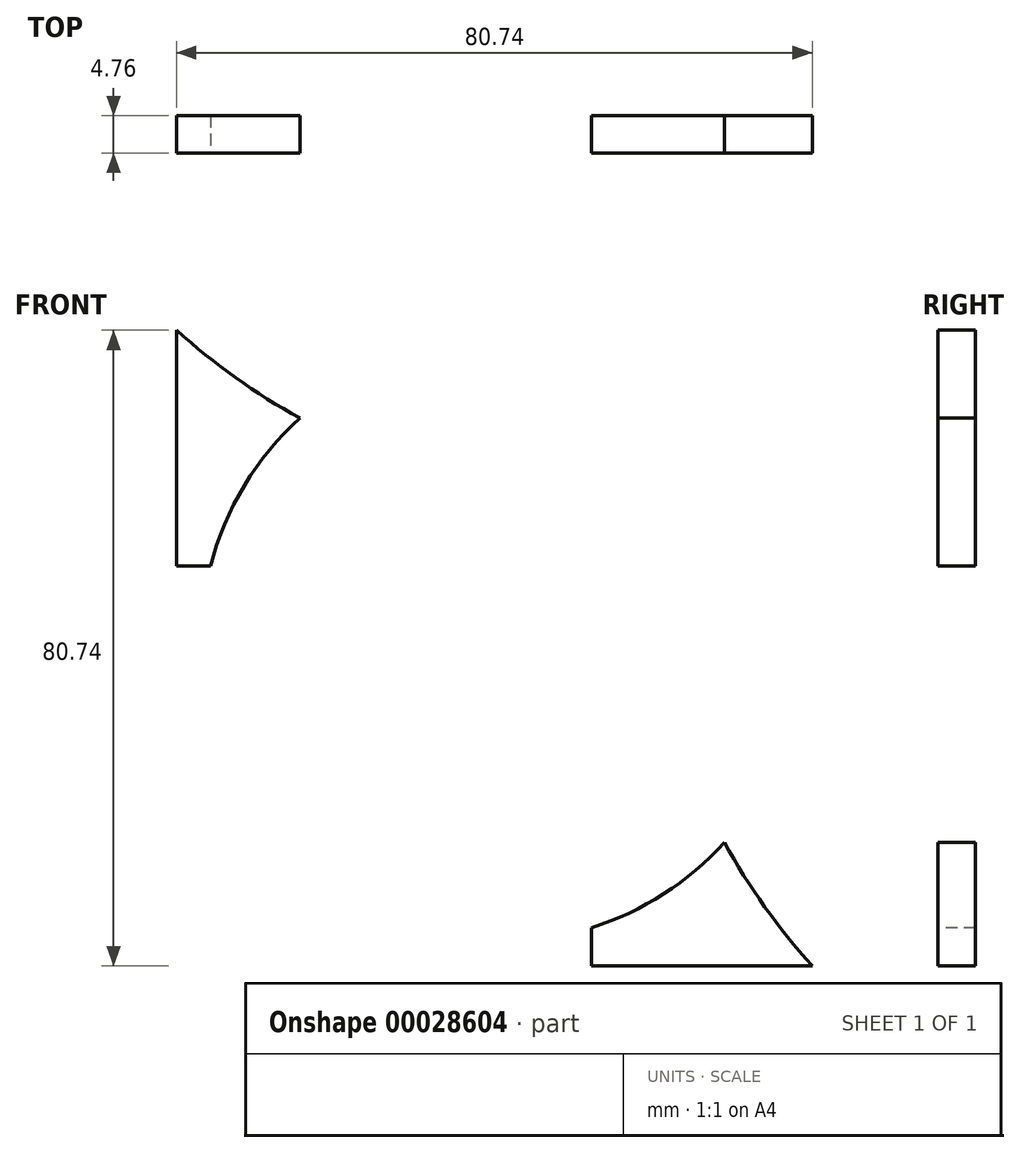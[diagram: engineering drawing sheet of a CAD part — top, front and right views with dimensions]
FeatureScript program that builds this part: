
annotation { "Feature Type Name" : "Feature", "Feature Type Description" : "" }
export const myFeature = defineFeature(function(context is Context, id is Id, definition is map)
    precondition{}
    {
        {
            var Q0;
            Q0=qCreatedBy(makeId("Front.planeOp"),FACE);
            var sketch = newSketch(context, id + "F0", { "sketchPlane" : qUnion([Q0])});
            skLineSegment(sketch, "E0.bottom", {"start": v(0, 0) * mm, "end": v(120.65, 0) * mm});
            skLineSegment(sketch, "E0.top", {"start": v(0, 120.65) * mm, "end": v(25.4, 120.65) * mm});
            skLineSegment(sketch, "E0.left", {"start": v(0, 0) * mm, "end": v(0, 120.65) * mm});
            skLineSegment(sketch, "E0.right", {"start": v(120.65, 0) * mm, "end": v(120.65, 25.4) * mm});
            skCircle(sketch, "E1", {"center": v(60.33, 60.33) * mm, "radius": 26.75 * mm});
            skArc(sketch, "E2", {"start": v(98.13, 65.62) * mm, "mid": v(87.32, 87.32) * mm, "end": v(65.62, 98.13) * mm});
            skArc(sketch, "E3", {"start": v(25.4, 120.65) * mm, "mid": v(43.4, 105.61) * mm, "end": v(65.62, 98.13) * mm});
            skArc(sketch, "E4", {"start": v(98.13, 65.62) * mm, "mid": v(105.61, 43.4) * mm, "end": v(120.65, 25.4) * mm});
            skPoint(sketch, "E5", {"position": v(25.4, 120.65) * mm});
            skPoint(sketch, "E6", {"position": v(120.65, 25.4) * mm});
            skSolve(sketch);
        }
        {
            var Q0;
            Q0=makeQuery(id+"F0.imprint","IMPRINT",FACE,{"disambiguationData":[TD([[makeQuery(id+"F0.imprint","IMPRINT",EDGE,{"derivedFrom":sQuery(id+"F0.wireOp",EDGE,"E0.bottom")}),1.0]])]});
            extrude(context, id + "F1", {"entities" : qUnion([Q0]), "depth" : 4.76 * mm});
        }
        {
            var Q0;
            Q0=makeQuery(id+"F1.opExtrude","CAP_FACE",FACE,{"disambiguationData":[OSD([sQuery(id+"F0.wireOp",EDGE,"E0.bottom"),sQuery(id+"F0.wireOp",EDGE,"E0.top"),sQuery(id+"F0.wireOp",EDGE,"E0.left"),sQuery(id+"F0.wireOp",EDGE,"E0.right"),sQuery(id+"F0.wireOp",EDGE,"E1"),sQuery(id+"F0.wireOp",EDGE,"E2"),sQuery(id+"F0.wireOp",EDGE,"E3"),sQuery(id+"F0.wireOp",EDGE,"E4")])],"isStart":false});
            var sketch = newSketch(context, id + "F2", { "sketchPlane" : qUnion([Q0])});
            skLineSegment(sketch, "E7", {"start": v(12.7, 114.3) * mm, "end": v(12.7, 12.7) * mm});
            skLineSegment(sketch, "E8", {"start": v(12.7, 12.7) * mm, "end": v(114.3, 12.7) * mm});
            skPoint(sketch, "E9", {"position": v(12.7, 88.9) * mm});
            skPoint(sketch, "E10", {"position": v(88.9, 12.7) * mm});
            skPoint(sketch, "E11", {"position": v(12.7, 63.5) * mm});
            skPoint(sketch, "E12", {"position": v(63.5, 12.7) * mm});
            skSolve(sketch);
        }
        {
            var Q0;
            Q0=sQuery(id+"F2.wireOp",VERTEX,"E9");
            var Q1;
            Q1=sQuery(id+"F2.wireOp",VERTEX,"E7.start");
            var Q2;
            Q2=sQuery(id+"F2.wireOp",VERTEX,"E11");
            var Q3;
            Q3=sQuery(id+"F2.wireOp",VERTEX,"E8.start");
            var Q4;
            Q4=sQuery(id+"F2.wireOp",VERTEX,"E12");
            var Q5;
            Q5=sQuery(id+"F2.wireOp",VERTEX,"E10");
            var Q6;
            Q6=sQuery(id+"F2.wireOp",VERTEX,"E8.end");
            var Q7;
            Q7=makeQuery(id+"F1.opExtrude","SWEPT_BODY",BODY,{"disambiguationData":[OSD([sQuery(id+"F0.wireOp",EDGE,"E0.bottom"),sQuery(id+"F0.wireOp",EDGE,"E0.top"),sQuery(id+"F0.wireOp",EDGE,"E0.left"),sQuery(id+"F0.wireOp",EDGE,"E0.right"),sQuery(id+"F0.wireOp",EDGE,"E1"),sQuery(id+"F0.wireOp",EDGE,"E2"),sQuery(id+"F0.wireOp",EDGE,"E3"),sQuery(id+"F0.wireOp",EDGE,"E4")])]});
            hole(context, id + "F3", {"style" : HoleStyle.SIMPLE, "holeDiameter" : 6.35 * mm, "endStyle" : HoleEndStyle.THROUGH, "locations" : qUnion([Q0, Q1, Q2, Q3, Q4, Q5, Q6]), "scope" : qUnion([Q7])});
        }
        {
            var Q0;
            Q0=makeQuery(id+"F1.opExtrude","CAP_FACE",FACE,{"disambiguationData":[OSD([sQuery(id+"F0.wireOp",EDGE,"E0.bottom"),sQuery(id+"F0.wireOp",EDGE,"E0.top"),sQuery(id+"F0.wireOp",EDGE,"E0.left"),sQuery(id+"F0.wireOp",EDGE,"E0.right"),sQuery(id+"F0.wireOp",EDGE,"E1"),sQuery(id+"F0.wireOp",EDGE,"E2"),sQuery(id+"F0.wireOp",EDGE,"E3"),sQuery(id+"F0.wireOp",EDGE,"E4")])],"isStart":false});
            var sketch = newSketch(context, id + "F4", { "sketchPlane" : qUnion([Q0])});
            skCircle(sketch, "E13.cCircle", {"center": v(60.33, 60.33) * mm, "radius": 26.4 * mm, "construction": true});
            skLineSegment(sketch, "E13.0", {"start": v(81.36, 38.26) * mm, "end": v(51.74, 31.08) * mm});
            skLineSegment(sketch, "E13.1", {"start": v(51.74, 31.08) * mm, "end": v(30.7, 53.14) * mm});
            skLineSegment(sketch, "E13.2", {"start": v(30.7, 53.14) * mm, "end": v(39.3, 82.39) * mm});
            skLineSegment(sketch, "E13.3", {"start": v(39.3, 82.39) * mm, "end": v(68.91, 89.57) * mm});
            skLineSegment(sketch, "E13.4", {"start": v(68.91, 89.57) * mm, "end": v(89.95, 67.5) * mm});
            skLineSegment(sketch, "E13.5", {"start": v(89.95, 67.5) * mm, "end": v(81.36, 38.26) * mm});
            skPoint(sketch, "E13.0.midPoint", {"position": v(66.55, 34.67) * mm});
            skSolve(sketch);
        }
        {
            var Q0;
            Q0=sQuery(id+"F4.wireOp",VERTEX,"E13.1.end");
            var Q1;
            Q1=sQuery(id+"F4.wireOp",VERTEX,"E13.0.end");
            var Q2;
            Q2=sQuery(id+"F4.wireOp",VERTEX,"E13.5.end");
            var Q3;
            Q3=sQuery(id+"F4.wireOp",VERTEX,"E13.4.end");
            var Q4;
            Q4=sQuery(id+"F4.wireOp",VERTEX,"E13.3.end");
            var Q5;
            Q5=sQuery(id+"F4.wireOp",VERTEX,"E13.2.end");
            var Q6;
            Q6=makeQuery(id+"F1.opExtrude","SWEPT_BODY",BODY,{"disambiguationData":[OSD([sQuery(id+"F0.wireOp",EDGE,"E0.bottom"),sQuery(id+"F0.wireOp",EDGE,"E0.top"),sQuery(id+"F0.wireOp",EDGE,"E0.left"),sQuery(id+"F0.wireOp",EDGE,"E0.right"),sQuery(id+"F0.wireOp",EDGE,"E1"),sQuery(id+"F0.wireOp",EDGE,"E2"),sQuery(id+"F0.wireOp",EDGE,"E3"),sQuery(id+"F0.wireOp",EDGE,"E4")])]});
            hole(context, id + "F5", {"style" : HoleStyle.SIMPLE, "holeDiameter" : 4.3 * mm, "endStyle" : HoleEndStyle.THROUGH, "locations" : qUnion([Q0, Q1, Q2, Q3, Q4, Q5]), "scope" : qUnion([Q6])});
        }
        {
            var Q0;
            Q0=makeQuery(id+"F1.opExtrude","CAP_FACE",FACE,{"disambiguationData":[OSD([sQuery(id+"F0.wireOp",EDGE,"E0.bottom"),sQuery(id+"F0.wireOp",EDGE,"E0.top"),sQuery(id+"F0.wireOp",EDGE,"E0.left"),sQuery(id+"F0.wireOp",EDGE,"E0.right"),sQuery(id+"F0.wireOp",EDGE,"E1"),sQuery(id+"F0.wireOp",EDGE,"E2"),sQuery(id+"F0.wireOp",EDGE,"E3"),sQuery(id+"F0.wireOp",EDGE,"E4")])],"isStart":false});
            var sketch = newSketch(context, id + "F6", { "sketchPlane" : qUnion([Q0])});
            skArc(sketch, "E14.1", {"start": v(34.72, 88.64) * mm, "mid": v(26.56, 93.76) * mm, "end": v(19.05, 99.79) * mm});
            skArc(sketch, "E14.3", {"start": v(99.79, 19.05) * mm, "mid": v(93.76, 26.56) * mm, "end": v(88.64, 34.72) * mm});
            skLineSegment(sketch, "E14.5", {"start": v(19.05, 99.79) * mm, "end": v(19.05, 69.85) * mm});
            skLineSegment(sketch, "E14.6", {"start": v(19.05, 19.05) * mm, "end": v(52.7, 19.05) * mm});
            skArc(sketch, "E15", {"start": v(23.36, 50.8) * mm, "mid": v(34.03, 32.65) * mm, "end": v(52.7, 22.92) * mm});
            skLineSegment(sketch, "E16.bottom", {"start": v(23.36, 50.8) * mm, "end": v(19.05, 50.8) * mm});
            skLineSegment(sketch, "E16.top", {"start": v(23.36, 69.85) * mm, "end": v(19.05, 69.85) * mm});
            skLineSegment(sketch, "E17.left", {"start": v(52.7, 22.92) * mm, "end": v(52.7, 19.05) * mm});
            skLineSegment(sketch, "E17.right", {"start": v(71.76, 23.9) * mm, "end": v(71.76, 19.05) * mm});
            skLineSegment(sketch, "E18.trimOffspring", {"start": v(19.05, 50.8) * mm, "end": v(19.05, 19.05) * mm});
            skArc(sketch, "E19.trimOffspring", {"start": v(71.76, 23.9) * mm, "mid": v(80.92, 28.18) * mm, "end": v(88.64, 34.72) * mm});
            skLineSegment(sketch, "E20.trimOffspring", {"start": v(71.76, 19.05) * mm, "end": v(99.79, 19.05) * mm});
            skArc(sketch, "E21.trimOffspring", {"start": v(34.72, 88.64) * mm, "mid": v(27.66, 80.08) * mm, "end": v(23.36, 69.85) * mm});
            skSolve(sketch);
        }
        {
            var Q0;
            Q0=makeQuery(id+"F6.imprint","IMPRINT",FACE,{"disambiguationData":[TD([[makeQuery(id+"F6.imprint","IMPRINT",EDGE,{"derivedFrom":sQuery(id+"F6.wireOp",EDGE,"E14.6")}),1.0]])]});
            var Q1;
            Q1=makeQuery(id+"F6.imprint","IMPRINT",FACE,{"disambiguationData":[TD([[makeQuery(id+"F6.imprint","IMPRINT",EDGE,{"derivedFrom":sQuery(id+"F6.wireOp",EDGE,"E14.1")}),1.0]])]});
            var Q2;
            Q2=makeQuery(id+"F6.imprint","IMPRINT",FACE,{"disambiguationData":[TD([[makeQuery(id+"F6.imprint","IMPRINT",EDGE,{"derivedFrom":sQuery(id+"F6.wireOp",EDGE,"E14.3")}),1.0]])]});
            extrude(context, id + "F7", {"entities" : qUnion([Q0, Q1, Q2]), "operationType" : NewBodyOperationType.REMOVE, "endBound" : BoundingType.THROUGH_ALL, "oppositeDirection" : true, "depth" : 25.4 * mm});
        }
    });
